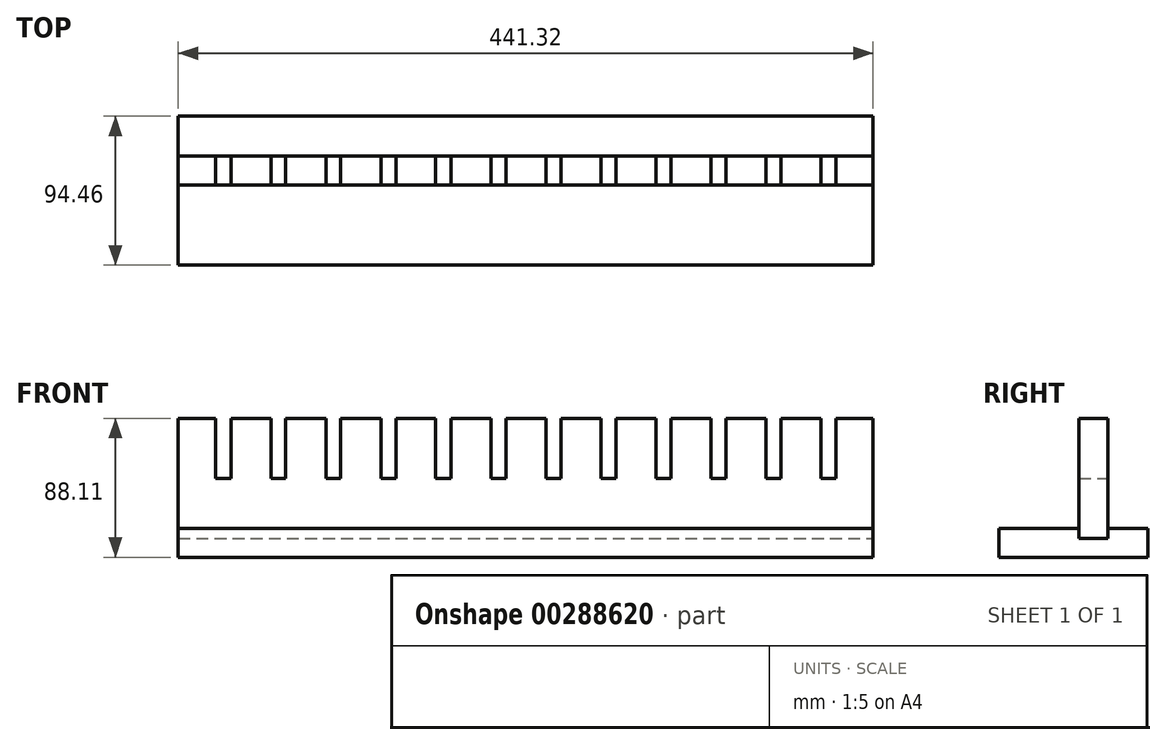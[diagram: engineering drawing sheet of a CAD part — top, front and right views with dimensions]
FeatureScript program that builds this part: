
annotation { "Feature Type Name" : "Feature", "Feature Type Description" : "" }
export const myFeature = defineFeature(function(context is Context, id is Id, definition is map)
    precondition{}
    {
        {
            var Q0;
            Q0=qCreatedBy(makeId("Front.planeOp"),FACE);
            var sketch = newSketch(context, id + "F0", { "sketchPlane" : qUnion([Q0])});
            skLineSegment(sketch, "E0.bottom", {"start": v(-220.66, 38.1) * mm, "end": v(-196.85, 38.1) * mm});
            skLineSegment(sketch, "E0.top", {"start": v(-220.66, -38.1) * mm, "end": v(220.66, -38.1) * mm});
            skLineSegment(sketch, "E0.left", {"start": v(-220.66, 38.1) * mm, "end": v(-220.66, -38.1) * mm});
            skLineSegment(sketch, "E0.right", {"start": v(220.66, 38.1) * mm, "end": v(220.66, -38.1) * mm});
            skLineSegment(sketch, "E1.top", {"start": v(-196.85, 0) * mm, "end": v(-187.32, 0) * mm});
            skLineSegment(sketch, "E1.left", {"start": v(-196.85, 38.1) * mm, "end": v(-196.85, 0) * mm});
            skLineSegment(sketch, "E1.right", {"start": v(-187.32, 38.1) * mm, "end": v(-187.32, 0) * mm});
            skLineSegment(sketch, "E2.1.0.0", {"start": v(-152.4, 38.1) * mm, "end": v(-152.4, 0) * mm});
            skLineSegment(sketch, "E2.1.0.1", {"start": v(-161.92, 38.1) * mm, "end": v(-161.92, 0) * mm});
            skLineSegment(sketch, "E2.1.0.2", {"start": v(-161.92, 0) * mm, "end": v(-152.4, 0) * mm});
            skLineSegment(sketch, "E2.2.0.0", {"start": v(-117.47, 38.1) * mm, "end": v(-117.47, 0) * mm});
            skLineSegment(sketch, "E2.2.0.1", {"start": v(-127, 38.1) * mm, "end": v(-127, 0) * mm});
            skLineSegment(sketch, "E2.2.0.2", {"start": v(-127, 0) * mm, "end": v(-117.47, 0) * mm});
            skLineSegment(sketch, "E2.3.0.0", {"start": v(-82.55, 38.1) * mm, "end": v(-82.55, 0) * mm});
            skLineSegment(sketch, "E2.3.0.1", {"start": v(-92.07, 38.1) * mm, "end": v(-92.07, 0) * mm});
            skLineSegment(sketch, "E2.3.0.2", {"start": v(-92.07, 0) * mm, "end": v(-82.55, 0) * mm});
            skLineSegment(sketch, "E2.4.0.0", {"start": v(-47.62, 38.1) * mm, "end": v(-47.62, 0) * mm});
            skLineSegment(sketch, "E2.4.0.1", {"start": v(-57.15, 38.1) * mm, "end": v(-57.15, 0) * mm});
            skLineSegment(sketch, "E2.4.0.2", {"start": v(-57.15, 0) * mm, "end": v(-47.62, 0) * mm});
            skLineSegment(sketch, "E2.5.0.0", {"start": v(-12.7, 38.1) * mm, "end": v(-12.7, 0) * mm});
            skLineSegment(sketch, "E2.5.0.1", {"start": v(-22.22, 38.1) * mm, "end": v(-22.22, 0) * mm});
            skLineSegment(sketch, "E2.5.0.2", {"start": v(-22.22, 0) * mm, "end": v(-12.7, 0) * mm});
            skLineSegment(sketch, "E2.6.0.0", {"start": v(22.23, 38.1) * mm, "end": v(22.23, 0) * mm});
            skLineSegment(sketch, "E2.6.0.1", {"start": v(12.7, 38.1) * mm, "end": v(12.7, 0) * mm});
            skLineSegment(sketch, "E2.6.0.2", {"start": v(12.7, 0) * mm, "end": v(22.23, 0) * mm});
            skLineSegment(sketch, "E2.7.0.0", {"start": v(57.15, 38.1) * mm, "end": v(57.15, 0) * mm});
            skLineSegment(sketch, "E2.7.0.1", {"start": v(47.63, 38.1) * mm, "end": v(47.63, 0) * mm});
            skLineSegment(sketch, "E2.7.0.2", {"start": v(47.63, 0) * mm, "end": v(57.15, 0) * mm});
            skLineSegment(sketch, "E2.8.0.0", {"start": v(92.08, 38.1) * mm, "end": v(92.08, 0) * mm});
            skLineSegment(sketch, "E2.8.0.1", {"start": v(82.55, 38.1) * mm, "end": v(82.55, 0) * mm});
            skLineSegment(sketch, "E2.8.0.2", {"start": v(82.55, 0) * mm, "end": v(92.08, 0) * mm});
            skLineSegment(sketch, "E2.9.0.0", {"start": v(127, 38.1) * mm, "end": v(127, 0) * mm});
            skLineSegment(sketch, "E2.9.0.1", {"start": v(117.48, 38.1) * mm, "end": v(117.48, 0) * mm});
            skLineSegment(sketch, "E2.9.0.2", {"start": v(117.48, 0) * mm, "end": v(127, 0) * mm});
            skLineSegment(sketch, "E2.direction1", {"start": v(-196.85, 0) * mm, "end": v(-161.92, 0) * mm, "construction": true});
            skLineSegment(sketch, "E3", {"start": v(-196.85, 0) * mm, "end": v(-220.66, 0) * mm, "construction": true});
            skLineSegment(sketch, "E4", {"start": v(-220.66, -31.75) * mm, "end": v(220.66, -31.75) * mm, "construction": true});
            skLineSegment(sketch, "E5.trimOffspring", {"start": v(-187.32, 38.1) * mm, "end": v(-161.92, 38.1) * mm});
            skLineSegment(sketch, "E6.trimOffspring", {"start": v(-152.4, 38.1) * mm, "end": v(-127, 38.1) * mm});
            skLineSegment(sketch, "E7.trimOffspring", {"start": v(-117.47, 38.1) * mm, "end": v(-92.07, 38.1) * mm});
            skLineSegment(sketch, "E8.trimOffspring", {"start": v(-82.55, 38.1) * mm, "end": v(-57.15, 38.1) * mm});
            skLineSegment(sketch, "E9.trimOffspring", {"start": v(-47.62, 38.1) * mm, "end": v(-22.22, 38.1) * mm});
            skLineSegment(sketch, "E10.trimOffspring", {"start": v(-12.7, 38.1) * mm, "end": v(12.7, 38.1) * mm});
            skLineSegment(sketch, "E11.trimOffspring", {"start": v(22.23, 38.1) * mm, "end": v(47.63, 38.1) * mm});
            skLineSegment(sketch, "E12.trimOffspring", {"start": v(57.15, 38.1) * mm, "end": v(82.55, 38.1) * mm});
            skLineSegment(sketch, "E13.trimOffspring", {"start": v(92.08, 38.1) * mm, "end": v(117.48, 38.1) * mm});
            skLineSegment(sketch, "E14.trimOffspring", {"start": v(127, 38.1) * mm, "end": v(152.4, 38.1) * mm});
            skLineSegment(sketch, "E15.0.10.0", {"start": v(161.93, 38.1) * mm, "end": v(161.93, 0) * mm});
            skLineSegment(sketch, "E15.3.10.0", {"start": v(152.4, 38.1) * mm, "end": v(152.4, 0) * mm});
            skLineSegment(sketch, "E15.6.10.0", {"start": v(152.4, 0) * mm, "end": v(161.93, 0) * mm});
            skLineSegment(sketch, "E15.0.11.0", {"start": v(196.85, 38.1) * mm, "end": v(196.85, 0) * mm});
            skLineSegment(sketch, "E15.3.11.0", {"start": v(187.33, 38.1) * mm, "end": v(187.33, 0) * mm});
            skLineSegment(sketch, "E15.6.11.0", {"start": v(187.33, 0) * mm, "end": v(196.85, 0) * mm});
            skLineSegment(sketch, "E16.trimOffspring", {"start": v(161.93, 38.1) * mm, "end": v(187.33, 38.1) * mm});
            skLineSegment(sketch, "E17.trimOffspring", {"start": v(196.85, 38.1) * mm, "end": v(220.66, 38.1) * mm});
            skSolve(sketch);
        }
        {
            var Q0;
            Q0=makeQuery(id+"F0.imprint","IMPRINT",FACE,{"disambiguationData":[TD([[makeQuery(id+"F0.imprint","IMPRINT",EDGE,{"derivedFrom":sQuery(id+"F0.wireOp",EDGE,"E0.bottom")}),-1.0]])]});
            extrude(context, id + "F1", {"entities" : qUnion([Q0]), "depth" : 18.26 * mm});
        }
        {
            var Q0;
            Q0=makeQuery(id+"F1.opExtrude","SWEPT_FACE",FACE,{"disambiguationData":[OSD([sQuery(id+"F0.wireOp",EDGE,"E0.right")])]});
            var sketch = newSketch(context, id + "F2", { "sketchPlane" : qUnion([Q0])});
            skLineSegment(sketch, "E18", {"start": v(0, -31.75) * mm, "end": v(0, -38.1) * mm});
            skLineSegment(sketch, "E19", {"start": v(0, -38.1) * mm, "end": v(-18.26, -38.1) * mm});
            skLineSegment(sketch, "E20", {"start": v(-18.26, -38.1) * mm, "end": v(-18.26, -31.75) * mm});
            skLineSegment(sketch, "E21", {"start": v(0, -31.75) * mm, "end": v(25.4, -31.75) * mm});
            skLineSegment(sketch, "E22", {"start": v(25.4, -31.75) * mm, "end": v(25.4, -50) * mm});
            skLineSegment(sketch, "E23", {"start": v(25.4, -50) * mm, "end": v(-69.06, -50) * mm});
            skLineSegment(sketch, "E24", {"start": v(-69.06, -50) * mm, "end": v(-69.06, -31.75) * mm});
            skLineSegment(sketch, "E25", {"start": v(-18.26, -31.75) * mm, "end": v(-69.06, -31.75) * mm});
            skSolve(sketch);
        }
        {
            var Q0;
            Q0=makeQuery(id+"F2.imprint","IMPRINT",FACE,{"disambiguationData":[TD([[makeQuery(id+"F2.imprint","IMPRINT",EDGE,{"derivedFrom":sQuery(id+"F2.wireOp",EDGE,"E18")}),1.0]])]});
            var Q1;
            Q1=makeQuery(id+"F1.opExtrude","SWEPT_FACE",FACE,{"disambiguationData":[OSD([sQuery(id+"F0.wireOp",EDGE,"E0.left")])]});
            extrude(context, id + "F3", {"entities" : qUnion([Q0]), "endBound" : BoundingType.UP_TO_SURFACE, "oppositeDirection" : true, "endBoundEntityFace" : qUnion([Q1]), "depth" : 25.4 * mm});
        }
    });
